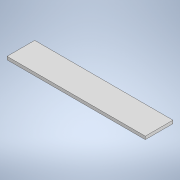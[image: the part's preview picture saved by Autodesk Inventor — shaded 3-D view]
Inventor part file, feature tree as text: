
AUTODESK INVENTOR PART (.ipt)
format: ipt  version: 2020 (Build 240168000, 168)  size: 92,160 bytes
history: native  units: mm
features: extrude x1, sketch x1
ambient origin geometry x8: Origin, YZ Plane, XZ Plane, XY Plane, X Axis, Y Axis, Z Axis, Center Point
bodies: Solide1 (feature_tree)
feature tree (2):
  extrude  "Extrusion1"  Depth=1000.0mm
  sketch  "Esquisse1"
